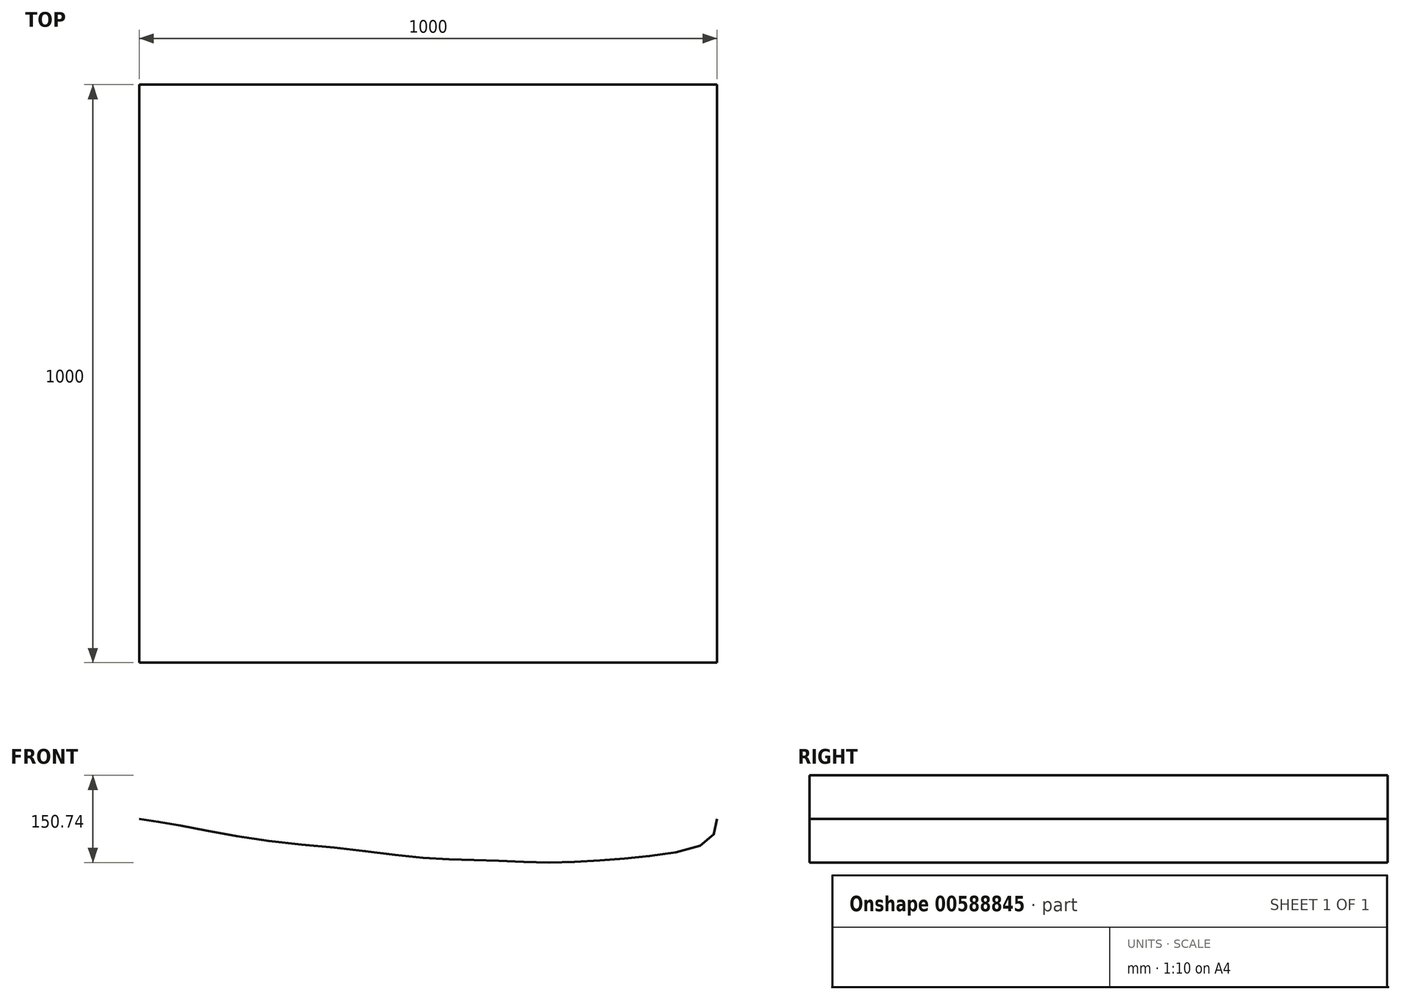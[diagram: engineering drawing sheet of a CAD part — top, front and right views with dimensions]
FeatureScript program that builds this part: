
annotation { "Feature Type Name" : "Feature", "Feature Type Description" : "" }
export const myFeature = defineFeature(function(context is Context, id is Id, definition is map)
    precondition{}
    {
        {
            var Q0;
            Q0=qCreatedBy(makeId("Front.planeOp"),FACE);
            var sketch = newSketch(context, id + "F0", { "sketchPlane" : qUnion([Q0])});
            skFitSpline(sketch, "E0", {"points": [v(500, -115.65) * mm, v(486.98, -151.94) * mm, v(400.8, -177.57) * mm, v(301.65, -187.35) * mm, v(199.93, -190.98) * mm, v(100.11, -187.23) * mm, v(-0.38, -183.55) * mm, v(-133.74, -168.4) * mm, v(-300.9, -150.5) * mm, v(-433.38, -126.44) * mm, v(-500, -115.65) * mm]});
            skFitSpline(sketch, "E1", {"points": [v(500, -115.65) * mm, v(486.98, -79.36) * mm, v(400.8, -53.72) * mm, v(301.65, -43.94) * mm, v(199.93, -40.32) * mm, v(100.11, -44.06) * mm, v(-0.38, -47.75) * mm, v(-133.74, -62.9) * mm, v(-300.9, -80.8) * mm, v(-433.38, -104.86) * mm, v(-500, -115.65) * mm]});
            skLineSegment(sketch, "E2", {"start": v(-500, -115.65) * mm, "end": v(0, 0) * mm, "construction": true});
            skSolve(sketch);
        }
        {
            var Q0;
            Q0=qSketchRegion(id+"F0",true);
            extrude(context, id + "F1", {"entities" : qUnion([Q0]), "oppositeDirection" : true, "depth" : 1000 * mm});
        }
        {
            var Q0;
            Q0=makeQuery(id+"F1.opExtrude","SWEPT_BODY",BODY,{"disambiguationData":[OSD([sQuery(id+"F0.wireOp",EDGE,"E0"),sQuery(id+"F0.wireOp",EDGE,"E1")])]});
            var Q1;
            Q1=sQuery(id+"F0.wireOp",EDGE,"E2");
            transform(context, id + "F2", {"entities" : qUnion([Q0]), "transformType" : TransformType.TRANSLATION_ENTITY, "oppositeDirectionEntity" : false, "transformLine" : qUnion([Q1]), "makeCopy" : false});
        }
    });
